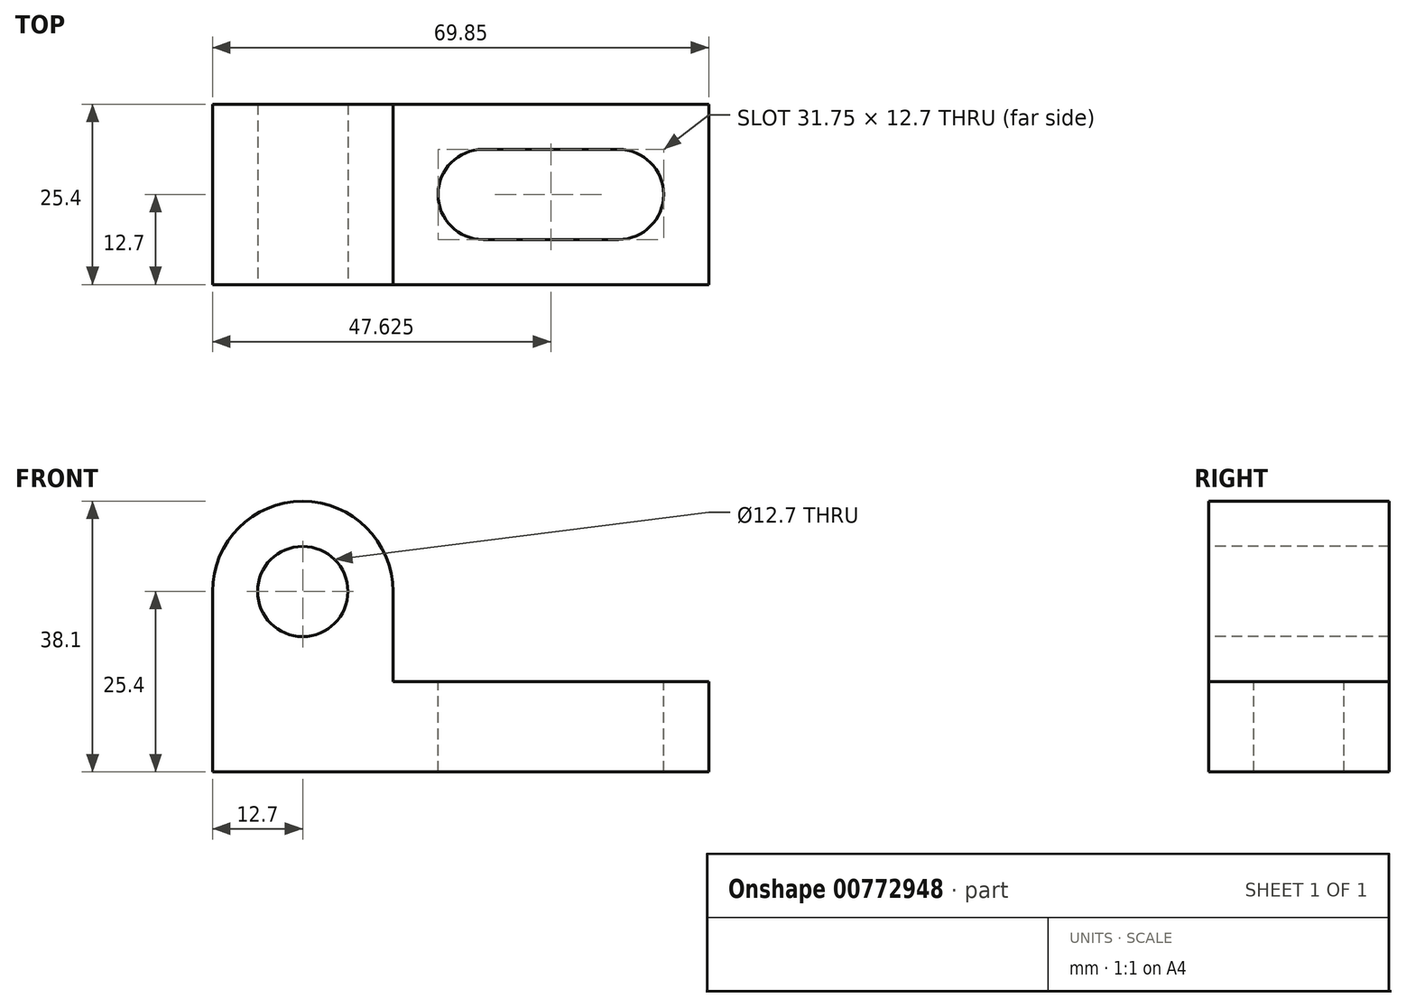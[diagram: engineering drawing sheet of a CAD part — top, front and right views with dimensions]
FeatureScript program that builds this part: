
annotation { "Feature Type Name" : "Feature", "Feature Type Description" : "" }
export const myFeature = defineFeature(function(context is Context, id is Id, definition is map)
    precondition{}
    {
        {
            var Q0;
            Q0=qCreatedBy(makeId("Front.planeOp"),FACE);
            var sketch = newSketch(context, id + "F0", { "sketchPlane" : qUnion([Q0])});
            skLineSegment(sketch, "E0", {"start": v(0, 0) * mm, "end": v(69.85, 0) * mm});
            skLineSegment(sketch, "E1", {"start": v(69.85, 0) * mm, "end": v(69.85, 38.1) * mm});
            skLineSegment(sketch, "E2", {"start": v(69.85, 38.1) * mm, "end": v(0, 38.1) * mm});
            skLineSegment(sketch, "E3", {"start": v(0, 38.1) * mm, "end": v(0, 0) * mm});
            skSolve(sketch);
        }
        {
            var Q0;
            Q0=makeQuery(id+"F0.imprint","IMPRINT",FACE,{"disambiguationData":[TD([[makeQuery(id+"F0.imprint","IMPRINT",EDGE,{"derivedFrom":sQuery(id+"F0.wireOp",EDGE,"E0")}),1.0]])]});
            extrude(context, id + "F1", {"entities" : qUnion([Q0]), "depth" : 25.4 * mm, "offsetDistance" : 25.4 * mm});
        }
        {
            var Q0;
            Q0=makeQuery(id+"F1.opExtrude","CAP_FACE",FACE,{"disambiguationData":[OSD([sQuery(id+"F0.wireOp",EDGE,"E0"),sQuery(id+"F0.wireOp",EDGE,"E1"),sQuery(id+"F0.wireOp",EDGE,"E2"),sQuery(id+"F0.wireOp",EDGE,"E3")])],"isStart":false});
            var sketch = newSketch(context, id + "F2", { "sketchPlane" : qUnion([Q0])});
            skLineSegment(sketch, "E4", {"start": v(25.4, 38.1) * mm, "end": v(25.4, 12.7) * mm});
            skLineSegment(sketch, "E5", {"start": v(25.4, 12.7) * mm, "end": v(69.85, 12.7) * mm});
            skLineSegment(sketch, "E6", {"start": v(69.85, 12.7) * mm, "end": v(69.85, 38.1) * mm});
            skLineSegment(sketch, "E7", {"start": v(69.85, 38.1) * mm, "end": v(25.4, 38.1) * mm});
            skSolve(sketch);
        }
        {
            var Q0;
            Q0=makeQuery(id+"F2.imprint","IMPRINT",FACE,{"disambiguationData":[TD([[makeQuery(id+"F2.imprint","IMPRINT",EDGE,{"derivedFrom":sQuery(id+"F2.wireOp",EDGE,"E4")}),1.0]])]});
            extrude(context, id + "F3", {"entities" : qUnion([Q0]), "operationType" : NewBodyOperationType.REMOVE, "oppositeDirection" : true, "depth" : 25.4 * mm, "offsetDistance" : 25.4 * mm});
        }
        {
            var Q0;
            Q0=makeQuery(id+"F1.opExtrude","CAP_FACE",FACE,{"disambiguationData":[OSD([sQuery(id+"F0.wireOp",EDGE,"E0"),sQuery(id+"F0.wireOp",EDGE,"E1"),sQuery(id+"F0.wireOp",EDGE,"E2"),sQuery(id+"F0.wireOp",EDGE,"E3")])],"isStart":false});
            var sketch = newSketch(context, id + "F4", { "sketchPlane" : qUnion([Q0])});
            skCircle(sketch, "E8", {"center": v(12.7, 25.4) * mm, "radius": 6.35 * mm});
            skSolve(sketch);
        }
        {
            var Q0;
            Q0=makeQuery(id+"F4.imprint","IMPRINT",FACE,{"disambiguationData":[TD([[makeQuery(id+"F4.imprint","IMPRINT",EDGE,{"derivedFrom":sQuery(id+"F4.wireOp",EDGE,"E8")}),1.0]])]});
            extrude(context, id + "F5", {"entities" : qUnion([Q0]), "operationType" : NewBodyOperationType.REMOVE, "oppositeDirection" : true, "depth" : 25.4 * mm, "offsetDistance" : 25.4 * mm});
        }
        {
            var Q0;
            Q0=makeQuery(id+"F1.opExtrude","CAP_FACE",FACE,{"disambiguationData":[OSD([sQuery(id+"F0.wireOp",EDGE,"E0"),sQuery(id+"F0.wireOp",EDGE,"E1"),sQuery(id+"F0.wireOp",EDGE,"E2"),sQuery(id+"F0.wireOp",EDGE,"E3")])],"isStart":false});
            var sketch = newSketch(context, id + "F6", { "sketchPlane" : qUnion([Q0])});
            skArc(sketch, "E9", {"start": v(25.4, 25.4) * mm, "mid": v(12.7, 38.1) * mm, "end": v(0, 25.4) * mm});
            skPoint(sketch, "E9.endSnap0", {"position": v(25.4, 25.4) * mm});
            skSolve(sketch);
        }
        {
            var Q0;
            {var subQ0=sQuery(id+"F6.wireOp",EDGE,"E9");var subQ1=makeQuery(id+"F1.opExtrude","CAP_EDGE",EDGE,{"disambiguationData":[OSD([sQuery(id+"F0.wireOp",EDGE,"E3")])],"isStart":false});var subQ2=makeQuery(id+"F6.imprint","INTERSECT",VERTEX,{"derivedFrom":[subQ1,subQ0]});Q0=makeQuery(id+"F6.imprint","IMPRINT",FACE,{"disambiguationData":[TD([[makeQuery(id+"F6.imprint","IMPRINT",EDGE,{"disambiguationData":[TD([[subQ2,1.0]])],"derivedFrom":subQ0}),-1.0]])]});}
            var Q1;
            {var subQ0=sQuery(id+"F6.wireOp",EDGE,"E9");var subQ1=makeQuery(id+"F3.boolean.opBoolean","COPY",EDGE,{"derivedFrom":makeQuery(id+"F3.opExtrude","CAP_EDGE",EDGE,{"disambiguationData":[OSD([sQuery(id+"F2.wireOp",EDGE,"E4")])],"isStart":true})});var subQ2=makeQuery(id+"F6.imprint","INTERSECT",VERTEX,{"derivedFrom":[subQ1,subQ0]});Q1=makeQuery(id+"F6.imprint","IMPRINT",FACE,{"disambiguationData":[TD([[makeQuery(id+"F6.imprint","IMPRINT",EDGE,{"disambiguationData":[TD([[subQ2,-1.0]])],"derivedFrom":subQ0}),-1.0]])]});}
            extrude(context, id + "F7", {"entities" : qUnion([Q0, Q1]), "operationType" : NewBodyOperationType.REMOVE, "oppositeDirection" : true, "depth" : 25.4 * mm, "offsetDistance" : 25.4 * mm});
        }
        {
            var Q0;
            Q0=makeQuery(id+"F3.boolean.opBoolean","COPY",FACE,{"derivedFrom":makeQuery(id+"F3.opExtrude","SWEPT_FACE",FACE,{"disambiguationData":[OSD([sQuery(id+"F2.wireOp",EDGE,"E5")])]})});
            var sketch = newSketch(context, id + "F8", { "sketchPlane" : qUnion([Q0])});
            skCircle(sketch, "E10", {"center": v(38.1, -12.7) * mm, "radius": 6.35 * mm});
            skCircle(sketch, "E11", {"center": v(57.15, -12.7) * mm, "radius": 6.35 * mm});
            skLineSegment(sketch, "E12", {"start": v(38.1, -19.05) * mm, "end": v(57.15, -19.05) * mm});
            skLineSegment(sketch, "E13", {"start": v(57.15, -19.05) * mm, "end": v(57.15, -6.35) * mm});
            skLineSegment(sketch, "E14", {"start": v(57.15, -6.35) * mm, "end": v(38.1, -6.35) * mm});
            skSolve(sketch);
        }
        {
            var Q0;
            {var subQ0=sQuery(id+"F8.wireOp",EDGE,"E10");var subQ1=makeQuery(id+"F8.imprint","INTERSECT",VERTEX,{"derivedFrom":[subQ0,sQuery(id+"F8.wireOp",EDGE,"E12")]});Q0=makeQuery(id+"F8.imprint","IMPRINT",FACE,{"disambiguationData":[TD([[makeQuery(id+"F8.imprint","IMPRINT",EDGE,{"disambiguationData":[TD([[subQ1,1.0]])],"derivedFrom":subQ0}),1.0]])]});}
            var Q1;
            {var subQ0=sQuery(id+"F8.wireOp",EDGE,"E12");Q1=makeQuery(id+"F8.imprint","IMPRINT",FACE,{"disambiguationData":[TD([[makeQuery(id+"F8.imprint","IMPRINT",EDGE,{"derivedFrom":subQ0}),1.0]])]});}
            var Q2;
            {var subQ0=sQuery(id+"F8.wireOp",EDGE,"E13");Q2=makeQuery(id+"F8.imprint","IMPRINT",FACE,{"disambiguationData":[TD([[makeQuery(id+"F8.imprint","IMPRINT",EDGE,{"derivedFrom":subQ0}),1.0]])]});}
            var Q3;
            {var subQ0=sQuery(id+"F8.wireOp",EDGE,"E13");Q3=makeQuery(id+"F8.imprint","IMPRINT",FACE,{"disambiguationData":[TD([[makeQuery(id+"F8.imprint","IMPRINT",EDGE,{"derivedFrom":subQ0}),-1.0]])]});}
            extrude(context, id + "F9", {"entities" : qUnion([Q0, Q1, Q2, Q3]), "operationType" : NewBodyOperationType.REMOVE, "oppositeDirection" : true, "depth" : 25.4 * mm, "offsetDistance" : 25.4 * mm});
        }
    });
